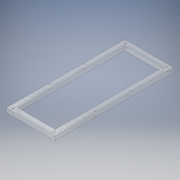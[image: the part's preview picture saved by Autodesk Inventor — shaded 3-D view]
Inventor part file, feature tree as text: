
AUTODESK INVENTOR PART (.ipt)
format: ipt  version: 2019 (Build 230136000, 136)  size: 135,168 bytes
history: native  units: mm
features: extrude x1, sketch x1
ambient origin geometry x8: Origin, YZ Plane, XZ Plane, XY Plane, X Axis, Y Axis, Z Axis, Center Point
bodies: Solid1 (feature_tree)
feature tree (2):
  extrude  "Extrusion1"  Depth=8.0mm
  sketch  "Sketch1"  dims[d0=8.0mm d1=8.0mm d2=70.0mm d3=170.0mm d4=6.0mm d5=0.0mm d6=1.8mm d7=1.8mm d8=57.75mm d9=33.0mm d10=25.0mm]
